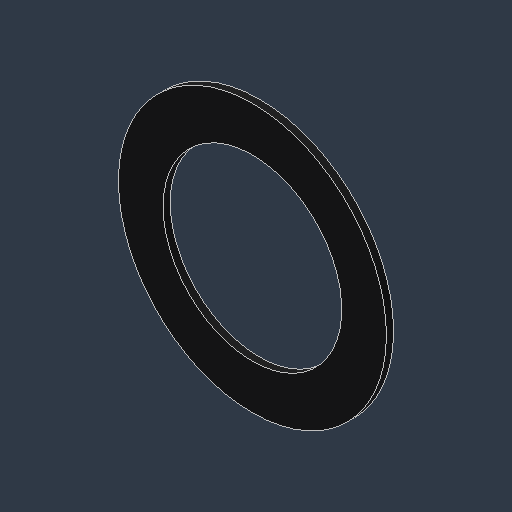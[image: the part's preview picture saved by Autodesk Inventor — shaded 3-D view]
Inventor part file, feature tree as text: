
AUTODESK INVENTOR PART (.ipt)
format: ipt  version: 2024.3 (Build 283343000, 343)  size: 88,064 bytes
history: native  units: mm (DEFAULTED — no unit token found)
features: revolve x1, sketch x1
ambient origin geometry x8: Origin, YZ Plane, XZ Plane, XY Plane, X Axis, Y Axis, Z Axis, Center Point
bodies: Solid1 (feature_tree)
feature tree (2):
  revolve  "Revolution1"  [1 undecoded]
  sketch  "Sketch2"  dims[d0=6.35mm d1=9.525mm d2=0.254mm d3=90.0deg]
note: 1 required parameter value undecoded (feature->parameter linkage not recoverable at this tier; creation-order binding heuristic only, values carry confidence <= 0.55)
